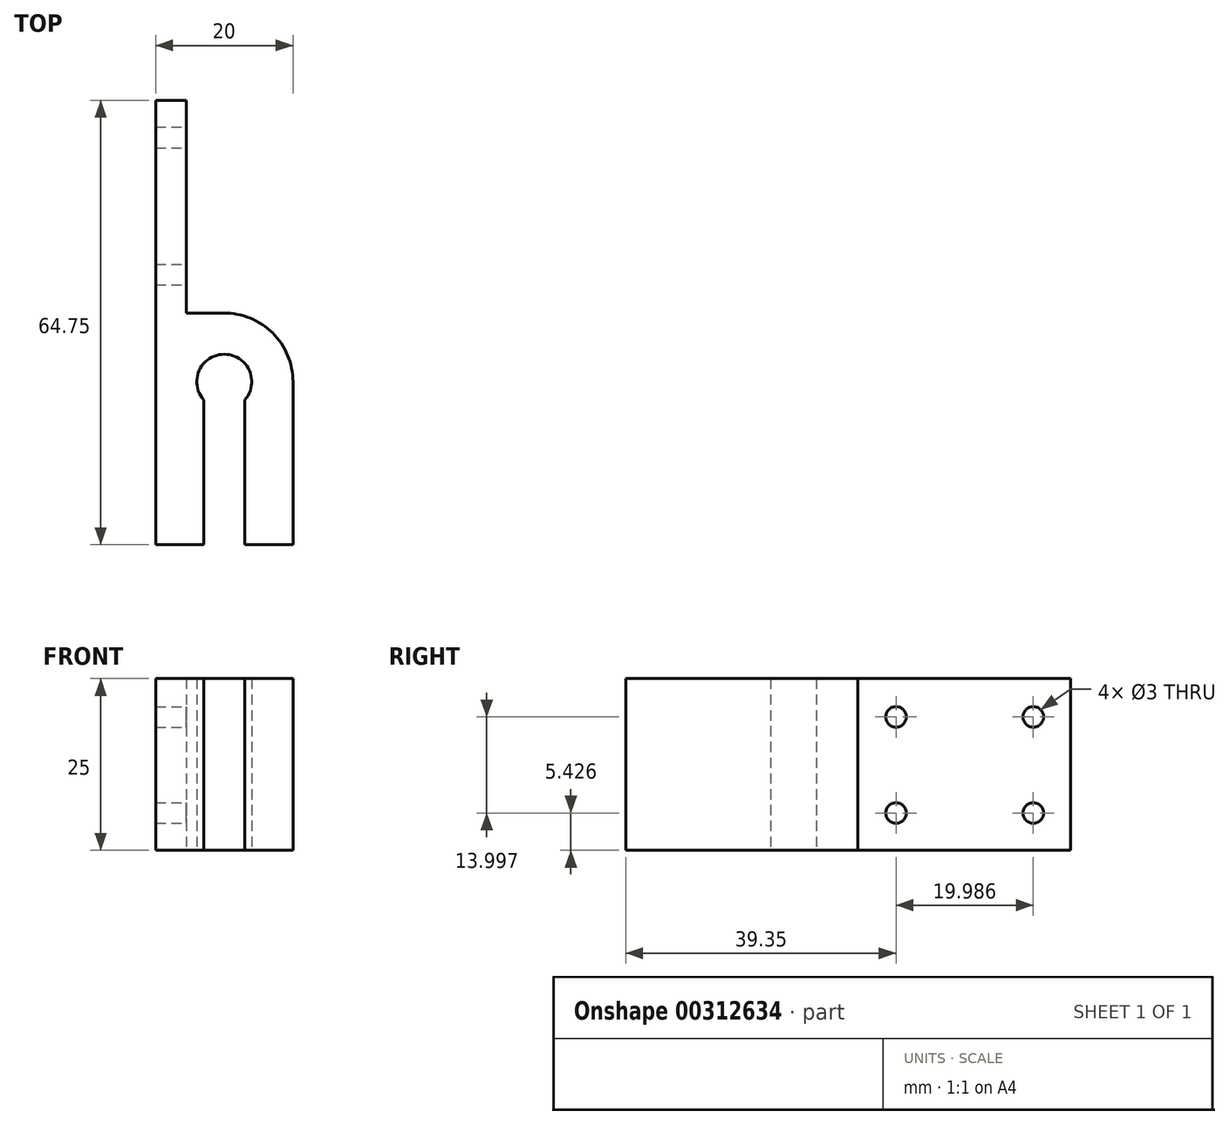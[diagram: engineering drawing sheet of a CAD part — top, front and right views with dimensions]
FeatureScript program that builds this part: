
annotation { "Feature Type Name" : "Feature", "Feature Type Description" : "" }
export const myFeature = defineFeature(function(context is Context, id is Id, definition is map)
    precondition{}
    {
        {
            var Q0;
            Q0=qCreatedBy(makeId("Top.planeOp"),FACE);
            var sketch = newSketch(context, id + "F0", { "sketchPlane" : qUnion([Q0])});
            skLineSegment(sketch, "E0.left", {"start": v(3.7, -23.75) * mm, "end": v(3.7, 23.75) * mm});
            skPoint(sketch, "E0.middle", {"position": v(0, 0) * mm});
            skLineSegment(sketch, "E1.bottom", {"start": v(3.7, 0) * mm, "end": v(9.7, 0) * mm});
            skLineSegment(sketch, "E1.top", {"start": v(3.7, -23.75) * mm, "end": v(10.7, -23.75) * mm});
            skLineSegment(sketch, "E1.left", {"start": v(3.7, 0) * mm, "end": v(3.7, -23.75) * mm});
            skLineSegment(sketch, "E1.right", {"start": v(23.7, 0) * mm, "end": v(23.7, -23.75) * mm});
            skLineSegment(sketch, "E2.top", {"start": v(3.7, 0.98) * mm, "end": v(3.75, 0.98) * mm});
            skLineSegment(sketch, "E2.left", {"start": v(3.7, 0) * mm, "end": v(3.7, 0.98) * mm});
            skArc(sketch, "E3", {"start": v(16.7, -2.65) * mm, "mid": v(13.7, 4) * mm, "end": v(10.7, -2.65) * mm});
            skArc(sketch, "E4", {"start": v(23.7, 0) * mm, "mid": v(20.74, 7.1) * mm, "end": v(13.6, 10) * mm});
            skLineSegment(sketch, "E5.top", {"start": v(10.3, -23.75) * mm, "end": v(10.7, -23.75) * mm});
            skLineSegment(sketch, "E6", {"start": v(16.7, -2.65) * mm, "end": v(16.7, -23.75) * mm});
            skLineSegment(sketch, "E7", {"start": v(10.7, -2.65) * mm, "end": v(10.7, -23.75) * mm});
            skLineSegment(sketch, "E8", {"start": v(13.8, 10) * mm, "end": v(8.2, 10) * mm});
            skLineSegment(sketch, "E9.top", {"start": v(3.7, 41) * mm, "end": v(8.2, 41) * mm});
            skLineSegment(sketch, "E9.left", {"start": v(3.7, 10) * mm, "end": v(3.7, 41) * mm});
            skLineSegment(sketch, "E9.right", {"start": v(8.2, 10) * mm, "end": v(8.2, 41) * mm});
            skLineSegment(sketch, "E10.trimOffspring", {"start": v(23.65, 0.98) * mm, "end": v(23.7, 0.98) * mm});
            skArc(sketch, "E11.trimOffspring", {"start": v(3.75, 0.98) * mm, "mid": v(3.71, 0.5) * mm, "end": v(3.7, 0) * mm});
            skLineSegment(sketch, "E12.trimOffspring", {"start": v(16.7, -23.75) * mm, "end": v(23.7, -23.75) * mm});
            skLineSegment(sketch, "E13.trimOffspring", {"start": v(17.7, 0) * mm, "end": v(23.7, 0) * mm});
            skSolve(sketch);
        }
        {
            var Q0;
            Q0 = qSketchRegion(id + "F0", true);
            extrude(context, id + "F1", {"entities" : qUnion([Q0]), "depth" : 25 * mm});
        }
        {
            var Q0;
            Q0=makeQuery(id+"F1.opExtrude","SWEPT_FACE",FACE,{"disambiguationData":[OSD([sQuery(id+"F0.wireOp",EDGE,"E0.left"),sQuery(id+"F0.wireOp",EDGE,"E1.left"),sQuery(id+"F0.wireOp",EDGE,"E2.left"),sQuery(id+"F0.wireOp",EDGE,"E9.left")])]});
            var sketch = newSketch(context, id + "F2", { "sketchPlane" : qUnion([Q0])});
            skLineSegment(sketch, "E14.bottom", {"start": v(-35.59, 5.43) * mm, "end": v(-15.6, 5.43) * mm});
            skLineSegment(sketch, "E14.top", {"start": v(-35.59, 19.42) * mm, "end": v(-15.6, 19.42) * mm});
            skLineSegment(sketch, "E14.left", {"start": v(-35.59, 5.43) * mm, "end": v(-35.59, 19.42) * mm});
            skLineSegment(sketch, "E14.right", {"start": v(-15.6, 5.43) * mm, "end": v(-15.6, 19.42) * mm});
            skCircle(sketch, "E15", {"center": v(-35.59, 5.43) * mm, "radius": 1.5 * mm});
            skCircle(sketch, "E16", {"center": v(-35.59, 19.42) * mm, "radius": 1.5 * mm});
            skCircle(sketch, "E17", {"center": v(-15.6, 19.42) * mm, "radius": 1.5 * mm});
            skCircle(sketch, "E18", {"center": v(-15.6, 5.43) * mm, "radius": 1.5 * mm});
            skSolve(sketch);
        }
        {
            var Q0;
            {var subQ0=sQuery(id+"F2.wireOp",EDGE,"E14.right");var subQ1=sQuery(id+"F2.wireOp",EDGE,"E14.bottom");var subQ2=makeQuery(id+"F2.imprint","INTERSECT",VERTEX,{"derivedFrom":[subQ1,subQ0]});Q0=makeQuery(id+"F2.imprint","IMPRINT",FACE,{"disambiguationData":[TD([[makeQuery(id+"F2.imprint","IMPRINT",EDGE,{"disambiguationData":[TD([[subQ2,1.0]])],"derivedFrom":subQ1}),-1.0]])]});}
            var Q1;
            {var subQ0=sQuery(id+"F2.wireOp",EDGE,"E14.left");var subQ1=sQuery(id+"F2.wireOp",EDGE,"E14.bottom");var subQ2=makeQuery(id+"F2.imprint","INTERSECT",VERTEX,{"derivedFrom":[subQ1,subQ0]});Q1=makeQuery(id+"F2.imprint","IMPRINT",FACE,{"disambiguationData":[TD([[makeQuery(id+"F2.imprint","IMPRINT",EDGE,{"disambiguationData":[TD([[subQ2,-1.0]])],"derivedFrom":subQ1}),-1.0]])]});}
            var Q2;
            {var subQ0=sQuery(id+"F2.wireOp",EDGE,"E14.right");var subQ1=sQuery(id+"F2.wireOp",EDGE,"E14.top");var subQ2=makeQuery(id+"F2.imprint","INTERSECT",VERTEX,{"derivedFrom":[subQ1,subQ0]});Q2=makeQuery(id+"F2.imprint","IMPRINT",FACE,{"disambiguationData":[TD([[makeQuery(id+"F2.imprint","IMPRINT",EDGE,{"disambiguationData":[TD([[subQ2,1.0]])],"derivedFrom":subQ1}),1.0]])]});}
            var Q3;
            {var subQ0=sQuery(id+"F2.wireOp",EDGE,"E14.right");var subQ1=sQuery(id+"F2.wireOp",EDGE,"E14.top");var subQ2=makeQuery(id+"F2.imprint","INTERSECT",VERTEX,{"derivedFrom":[subQ1,subQ0]});Q3=makeQuery(id+"F2.imprint","IMPRINT",FACE,{"disambiguationData":[TD([[makeQuery(id+"F2.imprint","IMPRINT",EDGE,{"disambiguationData":[TD([[subQ2,1.0]])],"derivedFrom":subQ1}),-1.0]])]});}
            var Q4;
            {var subQ0=sQuery(id+"F2.wireOp",EDGE,"E14.left");var subQ1=sQuery(id+"F2.wireOp",EDGE,"E14.top");var subQ2=makeQuery(id+"F2.imprint","INTERSECT",VERTEX,{"derivedFrom":[subQ1,subQ0]});Q4=makeQuery(id+"F2.imprint","IMPRINT",FACE,{"disambiguationData":[TD([[makeQuery(id+"F2.imprint","IMPRINT",EDGE,{"disambiguationData":[TD([[subQ2,-1.0]])],"derivedFrom":subQ1}),-1.0]])]});}
            var Q5;
            {var subQ0=sQuery(id+"F2.wireOp",EDGE,"E14.left");var subQ1=sQuery(id+"F2.wireOp",EDGE,"E14.top");var subQ2=makeQuery(id+"F2.imprint","INTERSECT",VERTEX,{"derivedFrom":[subQ1,subQ0]});Q5=makeQuery(id+"F2.imprint","IMPRINT",FACE,{"disambiguationData":[TD([[makeQuery(id+"F2.imprint","IMPRINT",EDGE,{"disambiguationData":[TD([[subQ2,-1.0]])],"derivedFrom":subQ1}),1.0]])]});}
            var Q6;
            {var subQ0=sQuery(id+"F2.wireOp",EDGE,"E14.left");var subQ1=sQuery(id+"F2.wireOp",EDGE,"E14.bottom");var subQ2=makeQuery(id+"F2.imprint","INTERSECT",VERTEX,{"derivedFrom":[subQ1,subQ0]});Q6=makeQuery(id+"F2.imprint","IMPRINT",FACE,{"disambiguationData":[TD([[makeQuery(id+"F2.imprint","IMPRINT",EDGE,{"disambiguationData":[TD([[subQ2,-1.0]])],"derivedFrom":subQ1}),1.0]])]});}
            var Q7;
            {var subQ0=sQuery(id+"F2.wireOp",EDGE,"E14.right");var subQ1=sQuery(id+"F2.wireOp",EDGE,"E14.bottom");var subQ2=makeQuery(id+"F2.imprint","INTERSECT",VERTEX,{"derivedFrom":[subQ1,subQ0]});Q7=makeQuery(id+"F2.imprint","IMPRINT",FACE,{"disambiguationData":[TD([[makeQuery(id+"F2.imprint","IMPRINT",EDGE,{"disambiguationData":[TD([[subQ2,1.0]])],"derivedFrom":subQ1}),1.0]])]});}
            var Q8;
            Q8=sQuery(id+"F2.wireOp",EDGE,"E15");
            var Q9;
            Q9=sQuery(id+"F2.wireOp",EDGE,"E16");
            var Q10;
            Q10=sQuery(id+"F2.wireOp",EDGE,"E17");
            var Q11;
            Q11=sQuery(id+"F2.wireOp",EDGE,"E18");
            extrude(context, id + "F3", {"entities" : qUnion([Q0, Q1, Q2, Q3, Q4, Q5, Q6, Q7]), "operationType" : NewBodyOperationType.REMOVE, "surfaceEntities" : qUnion([Q8, Q9, Q10, Q11]), "depth" : 25 * mm, "hasSecondDirection" : true, "secondDirectionOppositeDirection" : true, "secondDirectionDepth" : 25 * mm});
        }
    });
